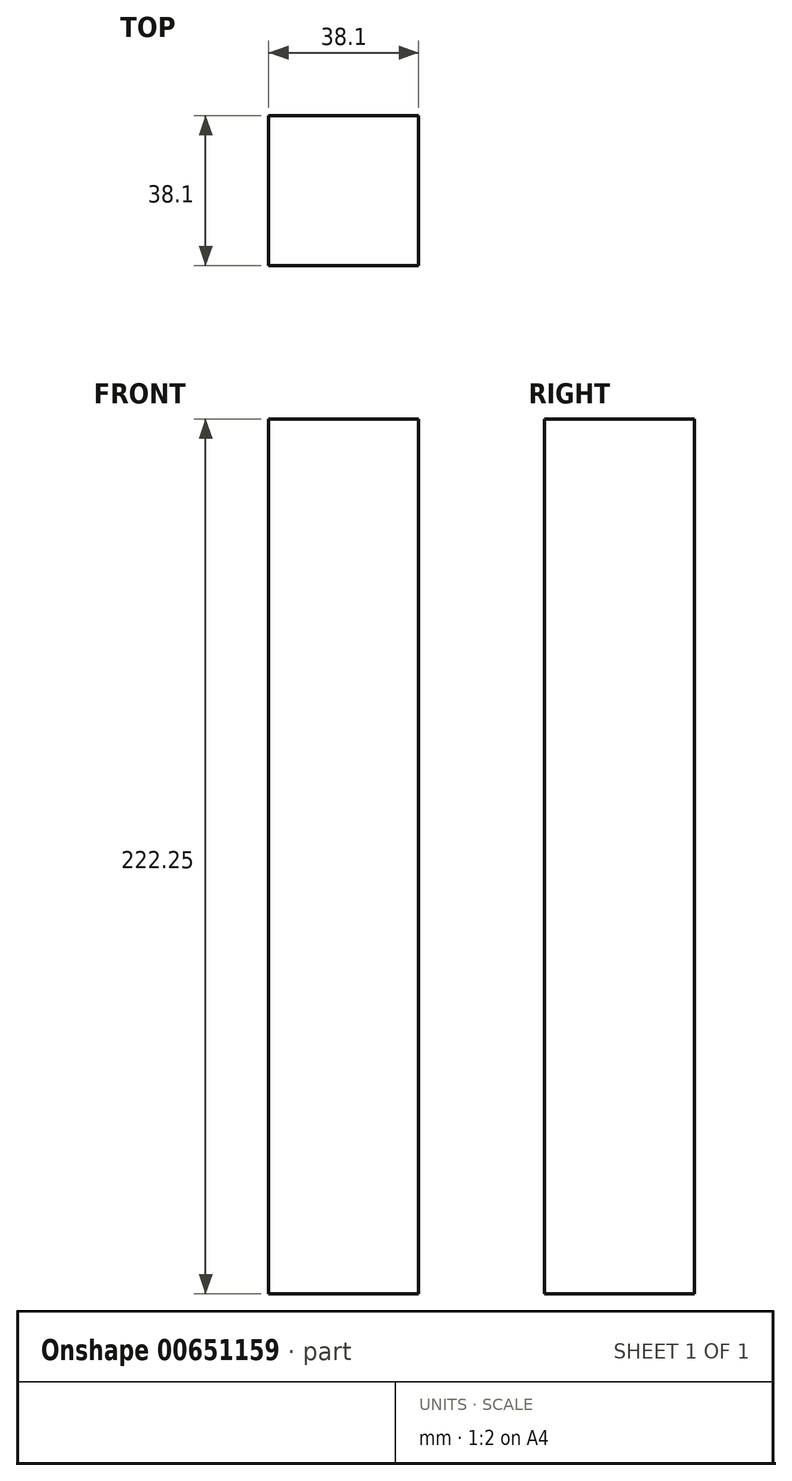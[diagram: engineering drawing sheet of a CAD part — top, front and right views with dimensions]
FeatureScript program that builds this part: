
annotation { "Feature Type Name" : "Feature", "Feature Type Description" : "" }
export const myFeature = defineFeature(function(context is Context, id is Id, definition is map)
    precondition{}
    {
        {
            var Q0;
            Q0=qCreatedBy(makeId("Top.planeOp"),FACE);
            var sketch = newSketch(context, id + "F0", { "sketchPlane" : qUnion([Q0])});
            skLineSegment(sketch, "E0.bottom", {"start": v(19.05, 19.05) * mm, "end": v(-19.05, 19.05) * mm});
            skLineSegment(sketch, "E0.top", {"start": v(19.05, -19.05) * mm, "end": v(-19.05, -19.05) * mm});
            skLineSegment(sketch, "E0.left", {"start": v(19.05, 19.05) * mm, "end": v(19.05, -19.05) * mm});
            skLineSegment(sketch, "E0.right", {"start": v(-19.05, 19.05) * mm, "end": v(-19.05, -19.05) * mm});
            skPoint(sketch, "E0.middle", {"position": v(0, 0) * mm});
            skSolve(sketch);
        }
        {
            var Q0;
            Q0=makeQuery(id+"F0.imprint","IMPRINT",FACE,{"disambiguationData":[TD([[makeQuery(id+"F0.imprint","IMPRINT",EDGE,{"derivedFrom":sQuery(id+"F0.wireOp",EDGE,"E0.bottom")}),1.0]])]});
            extrude(context, id + "F1", {"entities" : qUnion([Q0]), "depth" : 222.25 * mm, "offsetDistance" : 25.4 * mm});
        }
    });
